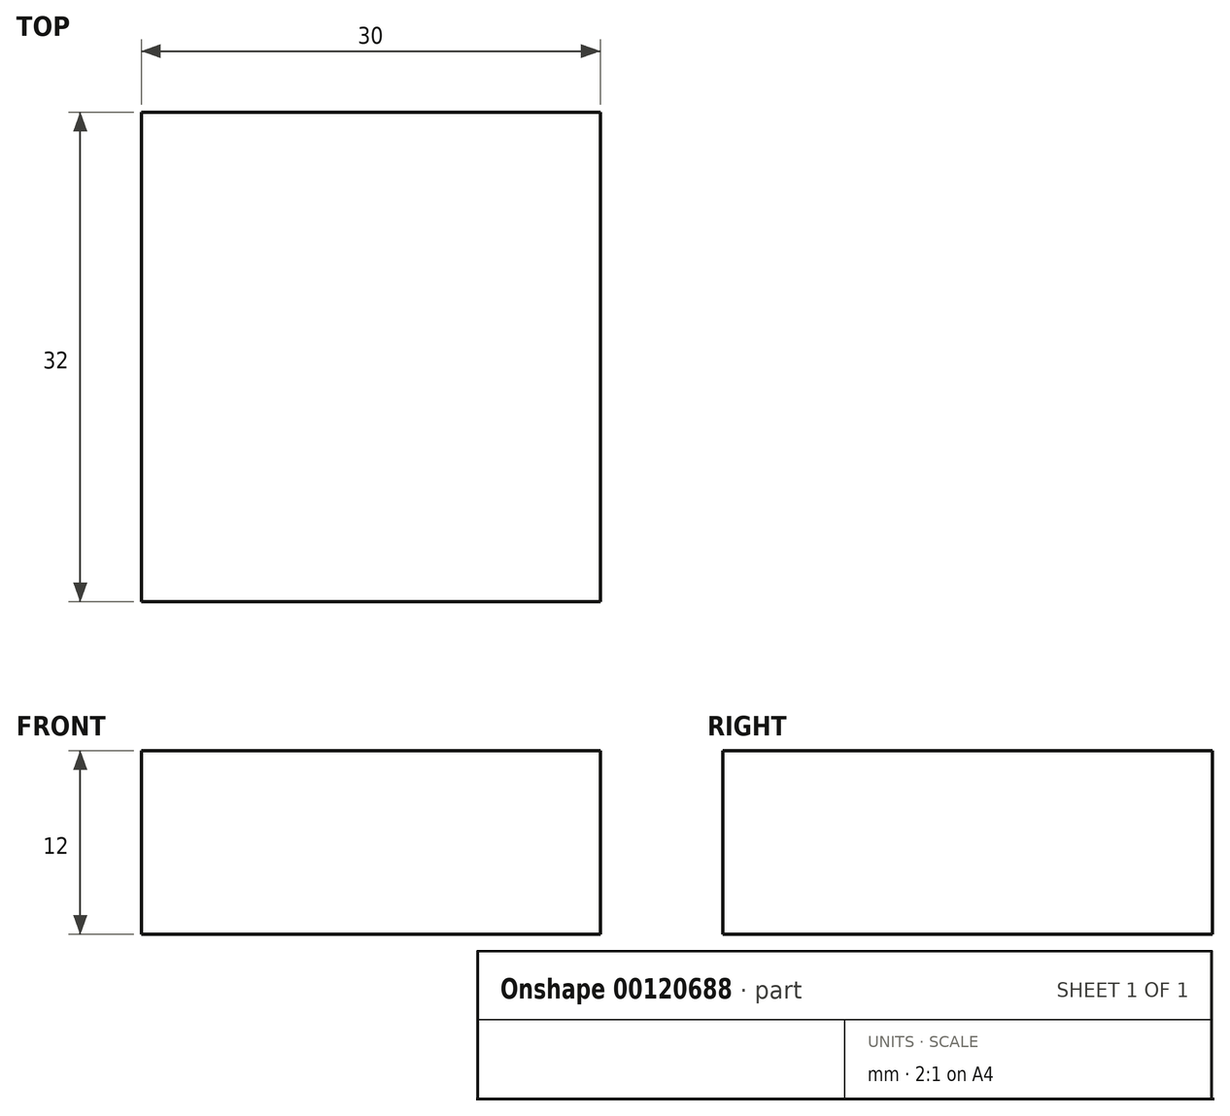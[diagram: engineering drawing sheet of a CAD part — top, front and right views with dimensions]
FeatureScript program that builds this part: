
annotation { "Feature Type Name" : "Feature", "Feature Type Description" : "" }
export const myFeature = defineFeature(function(context is Context, id is Id, definition is map)
    precondition{}
    {
        {
            var Q0;
            Q0=qCreatedBy(makeId("Top.planeOp"),FACE);
            var sketch = newSketch(context, id + "F0", { "sketchPlane" : qUnion([Q0])});
            skLineSegment(sketch, "E0.bottom", {"start": v(-23.51, 16.7) * mm, "end": v(6.49, 16.7) * mm});
            skLineSegment(sketch, "E0.top", {"start": v(-23.51, -15.3) * mm, "end": v(6.49, -15.3) * mm});
            skLineSegment(sketch, "E0.left", {"start": v(-23.51, 16.7) * mm, "end": v(-23.51, -15.3) * mm});
            skLineSegment(sketch, "E0.right", {"start": v(6.49, 16.7) * mm, "end": v(6.49, -15.3) * mm});
            skSolve(sketch);
        }
        {
            var Q0;
            Q0 = qSketchRegion(id + "F0", true);
            extrude(context, id + "F1", {"entities" : qUnion([Q0]), "depth" : 12 * mm});
        }
    });
